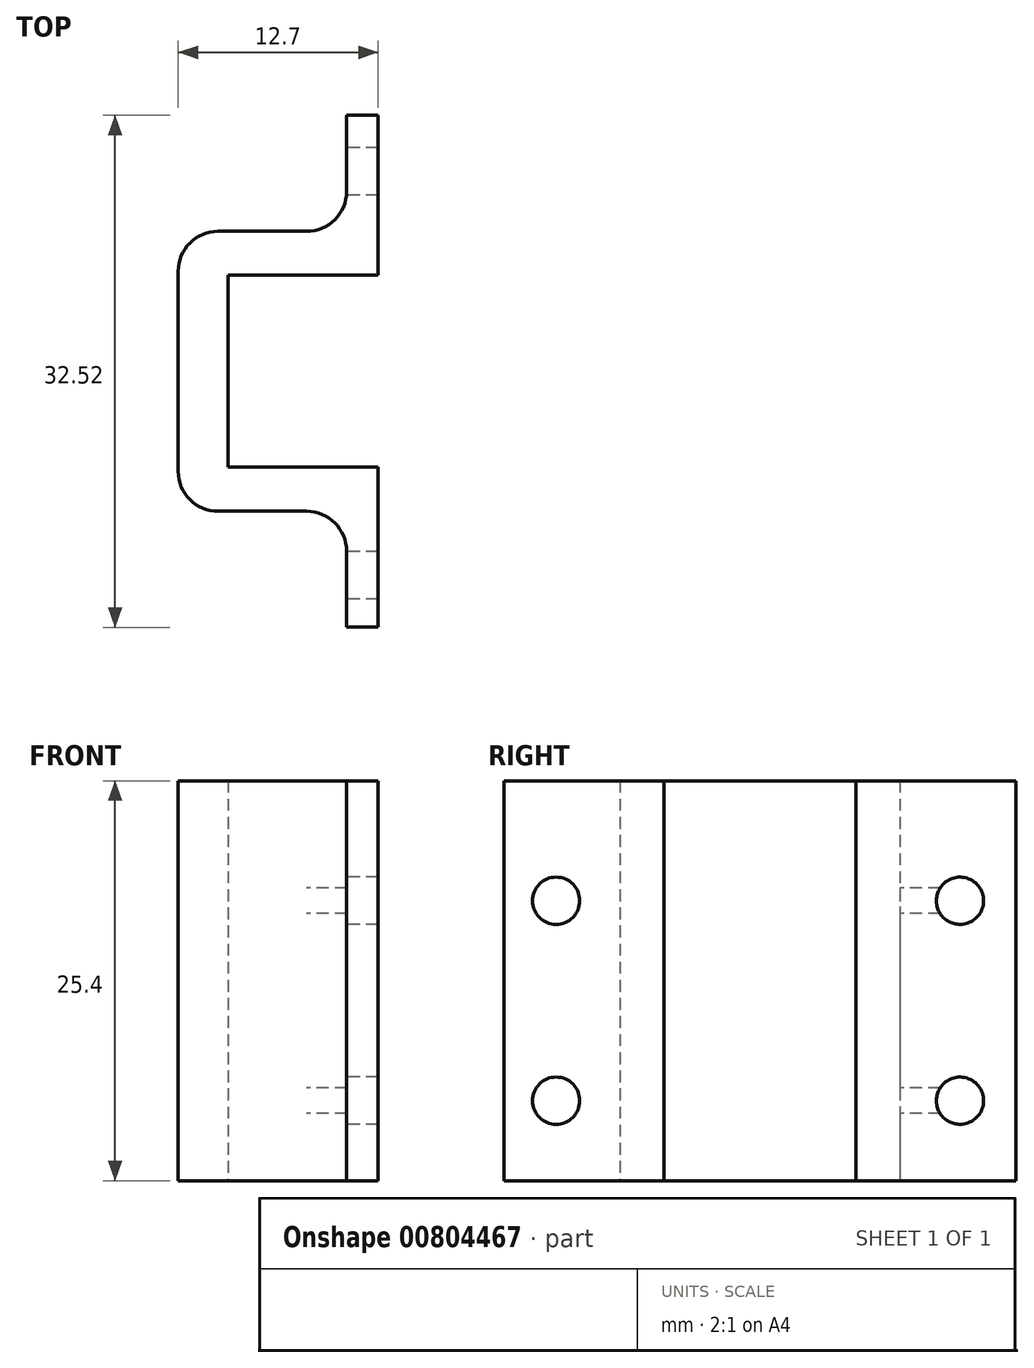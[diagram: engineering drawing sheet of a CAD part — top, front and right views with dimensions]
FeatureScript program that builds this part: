
annotation { "Feature Type Name" : "Feature", "Feature Type Description" : "" }
export const myFeature = defineFeature(function(context is Context, id is Id, definition is map)
    precondition{}
    {
        {
            var Q0;
            Q0=qCreatedBy(makeId("Top.planeOp"),FACE);
            var sketch = newSketch(context, id + "F0", { "sketchPlane" : qUnion([Q0])});
            skLineSegment(sketch, "E0", {"start": v(0, -7.37) * mm, "end": v(-2, -7.37) * mm});
            skLineSegment(sketch, "E1", {"start": v(-2, -7.37) * mm, "end": v(-2, 0) * mm});
            skLineSegment(sketch, "E2", {"start": v(-2, 0) * mm, "end": v(-12.7, 0) * mm});
            skLineSegment(sketch, "E3", {"start": v(-12.7, 0) * mm, "end": v(-12.7, 17.78) * mm});
            skLineSegment(sketch, "E4", {"start": v(-12.7, 17.78) * mm, "end": v(-2, 17.78) * mm});
            skLineSegment(sketch, "E5", {"start": v(-2, 17.78) * mm, "end": v(-2, 25.15) * mm});
            skLineSegment(sketch, "E6", {"start": v(-2, 25.15) * mm, "end": v(0, 25.15) * mm});
            skLineSegment(sketch, "E7", {"start": v(0, 25.15) * mm, "end": v(0, 14.99) * mm});
            skLineSegment(sketch, "E8", {"start": v(0, 14.99) * mm, "end": v(-9.52, 14.99) * mm});
            skLineSegment(sketch, "E9", {"start": v(-9.52, 14.99) * mm, "end": v(-9.52, 2.8) * mm});
            skLineSegment(sketch, "E10", {"start": v(-9.52, 2.8) * mm, "end": v(0, 2.8) * mm});
            skLineSegment(sketch, "E11", {"start": v(0, 2.8) * mm, "end": v(0, -7.37) * mm});
            skSolve(sketch);
        }
        {
            var Q0;
            Q0=makeQuery(id+"F0.imprint","IMPRINT",FACE,{"disambiguationData":[TD([[makeQuery(id+"F0.imprint","IMPRINT",EDGE,{"derivedFrom":sQuery(id+"F0.wireOp",EDGE,"E0")}),-1.0]])]});
            extrude(context, id + "F1", {"entities" : qUnion([Q0]), "depth" : 25.4 * mm, "offsetDistance" : 25.4 * mm});
        }
        {
            var Q0;
            Q0=makeQuery(id+"F1.opExtrude","SWEPT_FACE",FACE,{"disambiguationData":[OSD([sQuery(id+"F0.wireOp",EDGE,"E1")])]});
            var sketch = newSketch(context, id + "F2", { "sketchPlane" : qUnion([Q0])});
            skCircle(sketch, "E12", {"center": v(4.06, 5.08) * mm, "radius": 1.5 * mm});
            skCircle(sketch, "E13.1.0.0", {"center": v(4.06, 17.78) * mm, "radius": 1.5 * mm});
            skLineSegment(sketch, "E13.direction1", {"start": v(4.06, 5.08) * mm, "end": v(4.06, 17.78) * mm, "construction": true});
            skSolve(sketch);
        }
        {
            var Q0;
            Q0=makeQuery(id+"F1.opExtrude","SWEPT_FACE",FACE,{"disambiguationData":[OSD([sQuery(id+"F0.wireOp",EDGE,"E5")])]});
            var sketch = newSketch(context, id + "F3", { "sketchPlane" : qUnion([Q0])});
            skCircle(sketch, "E14", {"center": v(-21.59, 5.08) * mm, "radius": 1.5 * mm});
            skCircle(sketch, "E15.1.0.0", {"center": v(-21.59, 17.78) * mm, "radius": 1.5 * mm});
            skLineSegment(sketch, "E15.direction1", {"start": v(-21.59, 5.08) * mm, "end": v(-21.59, 17.78) * mm, "construction": true});
            skSolve(sketch);
        }
        {
            var Q0;
            Q0=makeQuery(id+"F2.imprint","IMPRINT",FACE,{"disambiguationData":[TD([[makeQuery(id+"F2.imprint","IMPRINT",EDGE,{"derivedFrom":sQuery(id+"F2.wireOp",EDGE,"E12")}),1.0]])]});
            var Q1;
            Q1=makeQuery(id+"F3.imprint","IMPRINT",FACE,{"disambiguationData":[TD([[makeQuery(id+"F3.imprint","IMPRINT",EDGE,{"derivedFrom":sQuery(id+"F3.wireOp",EDGE,"E14")}),1.0]])]});
            var Q2;
            Q2=makeQuery(id+"F3.imprint","IMPRINT",FACE,{"disambiguationData":[TD([[makeQuery(id+"F3.imprint","IMPRINT",EDGE,{"derivedFrom":sQuery(id+"F3.wireOp",EDGE,"E15.1.0.0")}),1.0]])]});
            var Q3;
            Q3=makeQuery(id+"F2.imprint","IMPRINT",FACE,{"disambiguationData":[TD([[makeQuery(id+"F2.imprint","IMPRINT",EDGE,{"derivedFrom":sQuery(id+"F2.wireOp",EDGE,"E13.1.0.0")}),1.0]])]});
            extrude(context, id + "F4", {"entities" : qUnion([Q0, Q1, Q2, Q3]), "operationType" : NewBodyOperationType.REMOVE, "oppositeDirection" : true, "depth" : 25.4 * mm, "offsetDistance" : 25.4 * mm});
        }
        {
            var Q0;
            Q0=makeQuery(id+"F1.opExtrude","SWEPT_EDGE",EDGE,{"disambiguationData":[OSD([sQuery(id+"F0.wireOp",EDGE,"E4"),sQuery(id+"F0.wireOp",EDGE,"E5")])]});
            var Q1;
            Q1=makeQuery(id+"F1.opExtrude","SWEPT_EDGE",EDGE,{"disambiguationData":[OSD([sQuery(id+"F0.wireOp",EDGE,"E1"),sQuery(id+"F0.wireOp",EDGE,"E2")])]});
            fillet(context, id + "F5", {"entities" : qUnion([Q0, Q1]), "radius" : 2.54 * mm, "tangentPropagation" : true, "allowEdgeOverflow" : false});
        }
        {
            var Q0;
            Q0=makeQuery(id+"F1.opExtrude","SWEPT_EDGE",EDGE,{"disambiguationData":[OSD([sQuery(id+"F0.wireOp",EDGE,"E2"),sQuery(id+"F0.wireOp",EDGE,"E3")])]});
            var Q1;
            Q1=makeQuery(id+"F1.opExtrude","SWEPT_EDGE",EDGE,{"disambiguationData":[OSD([sQuery(id+"F0.wireOp",EDGE,"E3"),sQuery(id+"F0.wireOp",EDGE,"E4")])]});
            fillet(context, id + "F6", {"entities" : qUnion([Q0, Q1]), "radius" : 2.54 * mm, "tangentPropagation" : true, "allowEdgeOverflow" : false});
        }
    });
